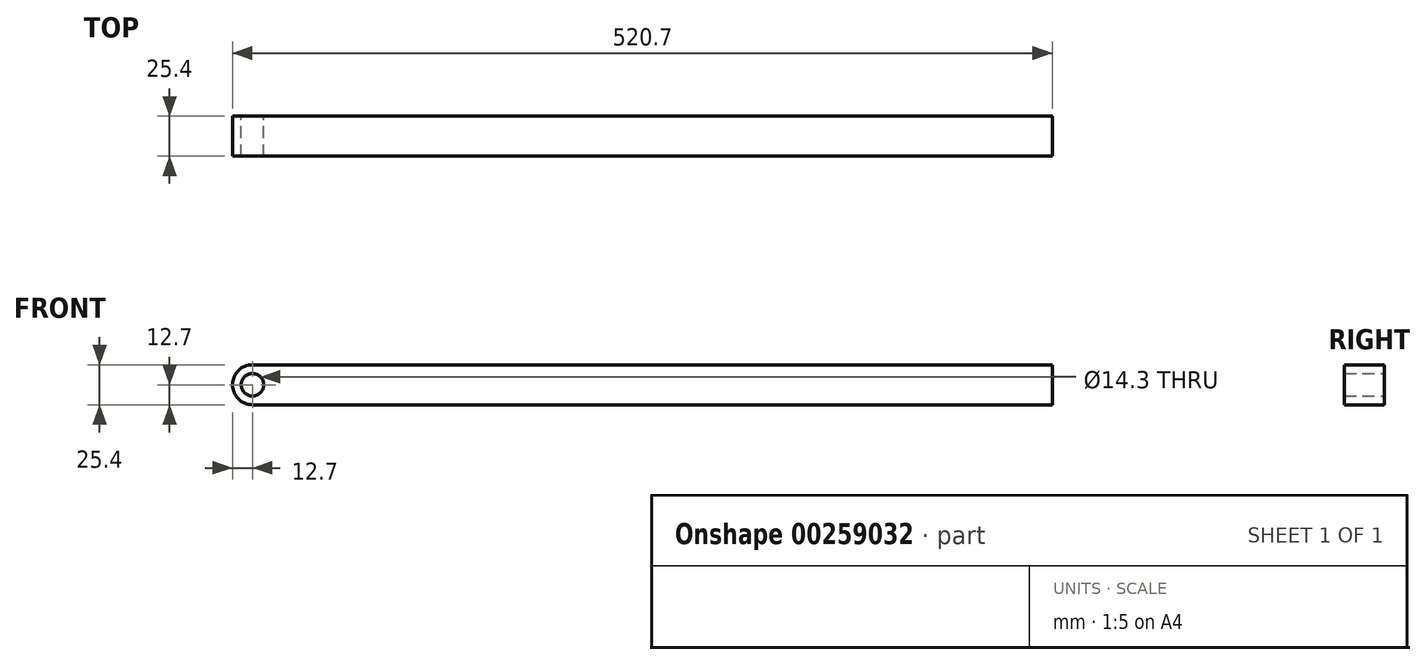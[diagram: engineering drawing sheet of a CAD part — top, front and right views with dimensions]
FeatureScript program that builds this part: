
annotation { "Feature Type Name" : "Feature", "Feature Type Description" : "" }
export const myFeature = defineFeature(function(context is Context, id is Id, definition is map)
    precondition{}
    {
        {
            var Q0;
            Q0=qCreatedBy(makeId("Front.planeOp"),FACE);
            var sketch = newSketch(context, id + "F0", { "sketchPlane" : qUnion([Q0])});
            skCircle(sketch, "E0", {"center": v(0, 0) * mm, "radius": 12.7 * mm});
            skCircle(sketch, "E1", {"center": v(0, 0) * mm, "radius": 7.15 * mm});
            skLineSegment(sketch, "E2", {"start": v(0, 12.7) * mm, "end": v(508, 12.7) * mm});
            skLineSegment(sketch, "E3", {"start": v(508, 12.7) * mm, "end": v(508, -12.7) * mm});
            skLineSegment(sketch, "E4", {"start": v(508, -12.7) * mm, "end": v(0, -12.7) * mm});
            skSolve(sketch);
        }
        {
            var Q0;
            {var subQ0=sQuery(id+"F0.wireOp",EDGE,"E2");Q0=makeQuery(id+"F0.imprint","IMPRINT",FACE,{"disambiguationData":[TD([[makeQuery(id+"F0.imprint","IMPRINT",EDGE,{"derivedFrom":subQ0}),-1.0]])]});}
            var Q1;
            Q1=makeQuery(id+"F0.imprint","IMPRINT",FACE,{"disambiguationData":[TD([[makeQuery(id+"F0.imprint","IMPRINT",EDGE,{"derivedFrom":sQuery(id+"F0.wireOp",EDGE,"E1")}),-1.0]])]});
            extrude(context, id + "F1", {"entities" : qUnion([Q0, Q1]), "depth" : 25.4 * mm});
        }
    });
